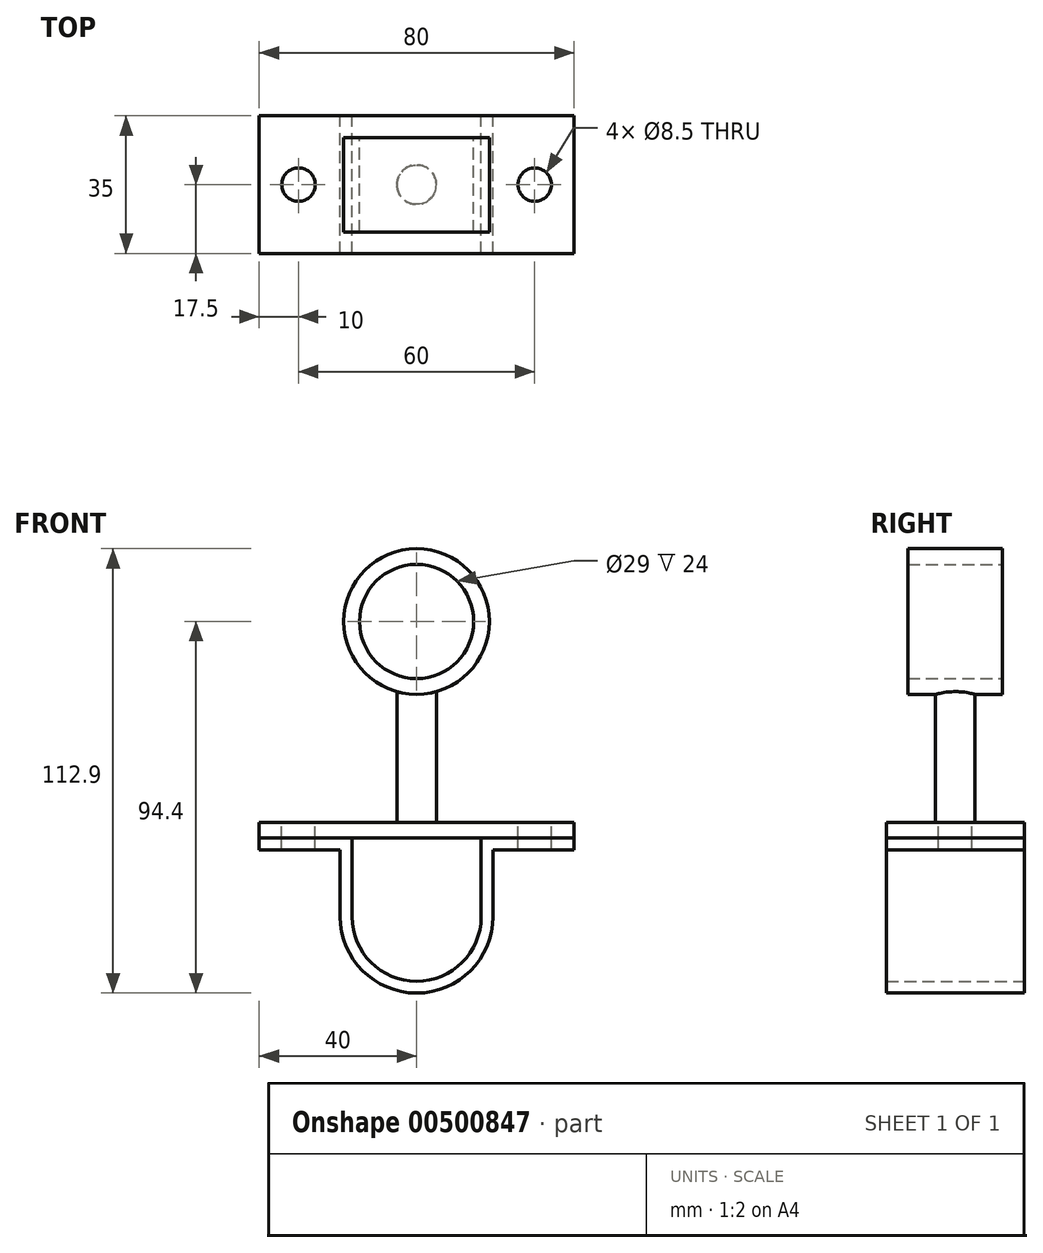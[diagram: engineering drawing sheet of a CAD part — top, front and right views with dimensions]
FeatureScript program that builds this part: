
annotation { "Feature Type Name" : "Feature", "Feature Type Description" : "" }
export const myFeature = defineFeature(function(context is Context, id is Id, definition is map)
    precondition{}
    {
        {
            var Q0;
            Q0=qCreatedBy(makeId("Front.planeOp"),FACE);
            var sketch = newSketch(context, id + "F0", { "sketchPlane" : qUnion([Q0])});
            skCircle(sketch, "E0", {"center": v(0, 0) * mm, "radius": 18.5 * mm});
            skCircle(sketch, "E1", {"center": v(0, 0) * mm, "radius": 14.5 * mm});
            skSolve(sketch);
        }
        {
            var Q0;
            Q0=makeQuery(id+"F0.imprint","IMPRINT",FACE,{"disambiguationData":[TD([[makeQuery(id+"F0.imprint","IMPRINT",EDGE,{"derivedFrom":sQuery(id+"F0.wireOp",EDGE,"E0")}),1.0]])]});
            extrude(context, id + "F1", {"entities" : qUnion([Q0]), "endBound" : BoundingType.SYMMETRIC, "depth" : 24 * mm, "offsetDistance" : 25 * mm});
        }
        {
            var Q0;
            Q0=qCreatedBy(makeId("Top.planeOp"),FACE);
            cPlane(context, id + "F2", {"entities" : qUnion([Q0]), "cplaneType" : CPlaneType.OFFSET, "offset" : 55 * mm, "oppositeDirection" : true, "width" : 150 * mm, "height" : 150 * mm});
        }
        {
            var Q0;
            Q0=qCreatedBy(id+"F2.planeOp",FACE);
            var sketch = newSketch(context, id + "F3", { "sketchPlane" : qUnion([Q0])});
            skCircle(sketch, "E2", {"center": v(0, 0) * mm, "radius": 5 * mm});
            skSolve(sketch);
        }
        {
            var Q0;
            Q0=makeQuery(id+"F3.imprint","IMPRINT",FACE,{"disambiguationData":[TD([[makeQuery(id+"F3.imprint","IMPRINT",EDGE,{"derivedFrom":sQuery(id+"F3.wireOp",EDGE,"E2")}),1.0]])]});
            extrude(context, id + "F4", {"entities" : qUnion([Q0]), "operationType" : NewBodyOperationType.ADD, "endBound" : BoundingType.UP_TO_NEXT, "depth" : 25 * mm, "offsetDistance" : 25 * mm});
        }
        {
            var Q0;
            Q0=qCreatedBy(id+"F2.planeOp",FACE);
            var sketch = newSketch(context, id + "F5", { "sketchPlane" : qUnion([Q0])});
            skLineSegment(sketch, "E3.bottom", {"start": v(-40, 17.5) * mm, "end": v(40, 17.5) * mm});
            skLineSegment(sketch, "E3.top", {"start": v(-40, -17.5) * mm, "end": v(40, -17.5) * mm});
            skLineSegment(sketch, "E3.left", {"start": v(-40, 17.5) * mm, "end": v(-40, -17.5) * mm});
            skLineSegment(sketch, "E3.right", {"start": v(40, 17.5) * mm, "end": v(40, -17.5) * mm});
            skPoint(sketch, "E3.middle", {"position": v(0, 0) * mm});
            skSolve(sketch);
        }
        {
            var Q0;
            Q0=makeQuery(id+"F5.imprint","IMPRINT",FACE,{"disambiguationData":[TD([[makeQuery(id+"F5.imprint","IMPRINT",EDGE,{"derivedFrom":sQuery(id+"F5.wireOp",EDGE,"E3.bottom")}),-1.0]])]});
            extrude(context, id + "F6", {"entities" : qUnion([Q0]), "operationType" : NewBodyOperationType.ADD, "depth" : 4 * mm, "offsetDistance" : 25 * mm});
        }
        {
            var Q0;
            Q0=qCreatedBy(makeId("Front.planeOp"),FACE);
            var sketch = newSketch(context, id + "F7", { "sketchPlane" : qUnion([Q0])});
            skPoint(sketch, "E4.0", {"position": v(0, -55) * mm});
            skLineSegment(sketch, "E5", {"start": v(0, -55) * mm, "end": v(0, -75) * mm, "construction": true});
            skLineSegment(sketch, "E6", {"start": v(0, -75) * mm, "end": v(-16.4, -75) * mm, "construction": true});
            skPoint(sketch, "E7.0", {"position": v(40, -55) * mm});
            skPoint(sketch, "E8.0", {"position": v(-40, -55) * mm});
            skLineSegment(sketch, "E9", {"start": v(0, -75) * mm, "end": v(-19.4, -75) * mm, "construction": true});
            skLineSegment(sketch, "E10.MirrorCS", {"start": v(0, -75) * mm, "end": v(19.4, -75) * mm, "construction": true});
            skLineSegment(sketch, "E11.MirrorCS", {"start": v(0, -75) * mm, "end": v(16.4, -75) * mm, "construction": true});
            skLineSegment(sketch, "E12", {"start": v(-16.4, -75) * mm, "end": v(-16.4, -55) * mm});
            skLineSegment(sketch, "E13", {"start": v(-19.4, -75) * mm, "end": v(-19.4, -58) * mm});
            skLineSegment(sketch, "E14", {"start": v(-19.4, -58) * mm, "end": v(-40, -58) * mm});
            skLineSegment(sketch, "E15", {"start": v(-16.4, -55) * mm, "end": v(-40, -55) * mm});
            skLineSegment(sketch, "E16.MirrorCS", {"start": v(19.4, -58) * mm, "end": v(40, -58) * mm});
            skLineSegment(sketch, "E17.MirrorCS", {"start": v(16.4, -55) * mm, "end": v(40, -55) * mm});
            skLineSegment(sketch, "E18.MirrorCS", {"start": v(16.4, -75) * mm, "end": v(16.4, -55) * mm});
            skLineSegment(sketch, "E19.MirrorCS", {"start": v(19.4, -75) * mm, "end": v(19.4, -58) * mm});
            skArc(sketch, "E20", {"start": v(-16.4, -75) * mm, "mid": v(0, -91.4) * mm, "end": v(16.4, -75) * mm});
            skArc(sketch, "E21", {"start": v(-19.4, -75) * mm, "mid": v(0, -94.4) * mm, "end": v(19.4, -75) * mm});
            skLineSegment(sketch, "E22", {"start": v(-40, -58) * mm, "end": v(-40, -55) * mm});
            skLineSegment(sketch, "E23", {"start": v(40, -58) * mm, "end": v(40, -55) * mm});
            skSolve(sketch);
        }
        {
            var Q0;
            Q0 = qSketchRegion(id + "F7", true);
            extrude(context, id + "F8", {"entities" : qUnion([Q0]), "endBound" : BoundingType.SYMMETRIC, "depth" : 35 * mm, "offsetDistance" : 25 * mm});
        }
        {
            var Q0;
            Q0=makeQuery(id+"F6.opExtrude","CAP_FACE",FACE,{"disambiguationData":[OSD([sQuery(id+"F5.wireOp",EDGE,"E3.bottom"),sQuery(id+"F5.wireOp",EDGE,"E3.top"),sQuery(id+"F5.wireOp",EDGE,"E3.left"),sQuery(id+"F5.wireOp",EDGE,"E3.right")])],"isStart":false});
            var sketch = newSketch(context, id + "F9", { "sketchPlane" : qUnion([Q0])});
            skPoint(sketch, "E24", {"position": v(30, 0) * mm});
            skPoint(sketch, "E25", {"position": v(-30, 0) * mm});
            skCircle(sketch, "E26", {"center": v(-30, 0) * mm, "radius": 4.25 * mm});
            skCircle(sketch, "E27.MirrorC", {"center": v(30, 0) * mm, "radius": 4.25 * mm});
            skSolve(sketch);
        }
        {
            var Q0;
            Q0 = qSketchRegion(id + "F9", true);
            extrude(context, id + "F10", {"entities" : qUnion([Q0]), "operationType" : NewBodyOperationType.REMOVE, "oppositeDirection" : true, "depth" : 25 * mm, "offsetDistance" : 25 * mm});
        }
    });
